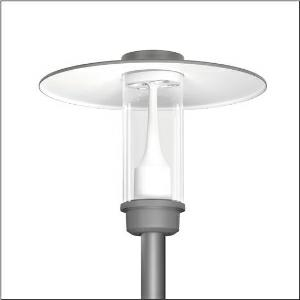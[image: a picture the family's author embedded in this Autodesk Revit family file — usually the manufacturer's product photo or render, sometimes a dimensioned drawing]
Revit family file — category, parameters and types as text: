
# Revit family: litepole_2_iq___p1_0a_5xa5425lf14h_94a7
name_source: partatom
category: Lighting Fixtures
units: mm (PartAtom-declared; Revit-internal decimal feet)

## family parameters
Cut with Voids When Loaded = No
Host = Face
Light Source = No
Part Type = Normal
Room Calculation Point = No
Round Connector Dimension = Use Diameter
Shared = No

## types (1)
- --- (1 x LED, 1520 lm, 10 W, 4000K)
    Apparent Load = 10 VA
    CIE Flux Codes = 33 62 89 96 100
    Color Rendering = 70
    Color Temperature = 4000K
    Default Elevation = 1800 mm
    Description = Litepole 2 iQ, mast luminaire, Module 540 iQ-SR, primary light control with 3 zone facetted reflector, of plastic, silver coated, highly specular, structured, primary optical cover: cover, of PMMA, transparent, light distribution: P1.0a, light emission: direct distribution, primary light characteristic: strongly asymmetric, installation type: post-top, LED, High Power LED, rated luminous flux: 1.520lm, luminous efficacy: 152lm/W, light colour: 740, colour temperature: 4000K, control gear: iQ Street-Remote, control: pre-setting: logarithmic dimming characteristic, Street-Remote, Auto-Match, Temp-Guard, Lumen-Switch, Night-Set, Smart-Wire, Light-Fading, Desk-Remote (wireless, voltage-free reading and setting of iQ features in the workshop via application-optimized NFC function/RFID function), optimised constant luminous flux control (CLO 2.0), with terminal, 6-pole, max. 2.5mm², mains connection: 230..240V, AC, 50/60Hz, start of lifetime: 10W, end of service life: 10W, reduction: 5W, luminaire housing, upper part, of aluminium, coated, Siteco® metallic grey (DB 702S), diameter: 750mm, height: 590mm, spigot size: d x l = 76 x 70mm (post-top) | with reducer (optional accessory) 60 x 70mm, mounting height: 3..5m, post-top mast mounting element, of diecast aluminium, coated, Siteco® metallic grey (DB 702S), Module 540 iQ-SR, traffic white (RAL 9016), equipment: standard, protection rating (complete): IP65, insulation class (complete): insulation class II (safety insulation), certification: CE, ENEC, VDE, packaging unit: 1 piece

Light Distribution: P1.0a
    Height = 590 mm
    Lamp = 1 x LED
    Lamp Light Flux = 1520 lm
    Lamp Power = 10 W
    Lamp count = 1
    Length = 750 mm
    Luminous efficacy = 152 lm/W
    Manufacturer = Siteco
    ModVariant = No
    Model = 5XA5425LF14H
    Number of Poles = 1
    OnlyDefault = Yes
    Power Factor = 1
    Product Name = Litepole 2 iQ | P1.0a
    Product group = mast luminaire | pylon top
    ProductGroupID = 6100
    Protection Class = Protection class II
    Protection Degree = IP 65
    RLX_Detail_Level = 1
    RLX_Emergency_Light_Flux = 0 lm
    RLX_Emergency_Type = 0
    RLX_Emergency_Type_DB = No
    RlxData = <blob elided: 59725 chars, md5=6db064d7>
    Socket = socket
    Standby Power = 0 W
    System Light Flux = 1520 lm
    System Power = 10 W
    Type Comments = factory setting: luminous flux: 100 % | dim-lin: 254 | 401 mA
    Type Image = l_1006518.jpg
    URL = http://relux.com
    VarID = @adj_189945
    Voltage = 0 V
    Weight = 0.00 kg
    Width = 0 mm  [stored 0 ft]

note: [stored X ft] marks values corroborated as IEEE doubles in the binary element streams (Revit-internal decimal feet)

## geometry (parser evidence)
native form markers: Blend x4, Sweep x11
no freeform markers — native parametric forms only
